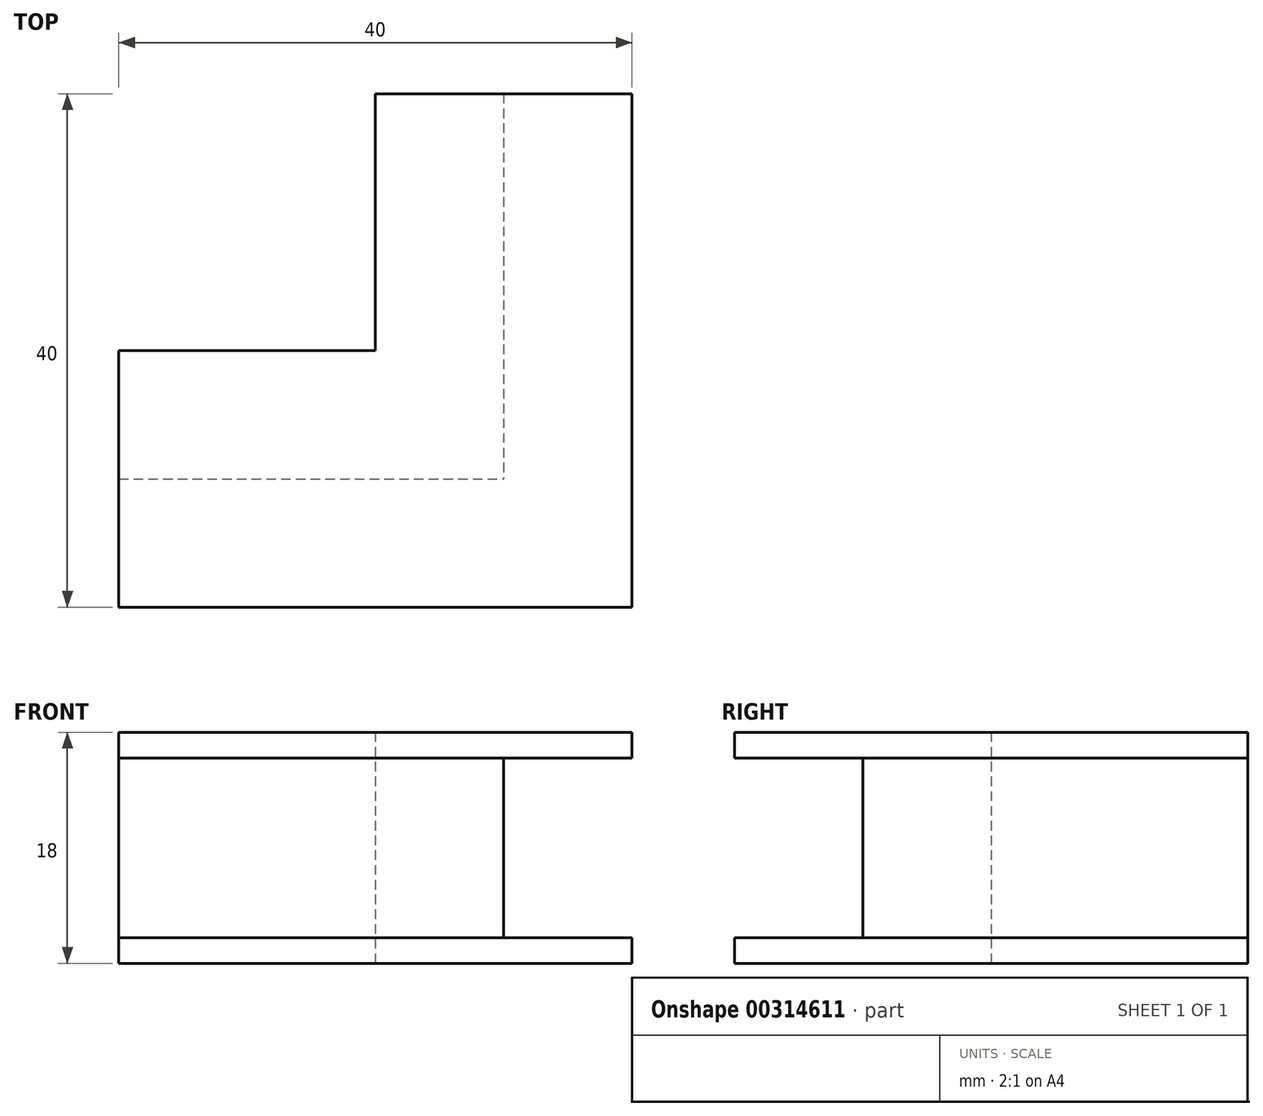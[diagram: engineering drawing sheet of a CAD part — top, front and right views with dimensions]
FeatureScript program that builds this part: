
annotation { "Feature Type Name" : "Feature", "Feature Type Description" : "" }
export const myFeature = defineFeature(function(context is Context, id is Id, definition is map)
    precondition{}
    {
        {
            var Q0;
            Q0=qCreatedBy(makeId("Top.planeOp"),FACE);
            var sketch = newSketch(context, id + "F0", { "sketchPlane" : qUnion([Q0])});
            skLineSegment(sketch, "E0", {"start": v(-10, 30) * mm, "end": v(0, 30) * mm});
            skLineSegment(sketch, "E1", {"start": v(0, 30) * mm, "end": v(0, 0) * mm});
            skLineSegment(sketch, "E2", {"start": v(0, 0) * mm, "end": v(-30, 0) * mm});
            skLineSegment(sketch, "E3", {"start": v(-30, 0) * mm, "end": v(-30, 10) * mm});
            skLineSegment(sketch, "E4", {"start": v(-30, 10) * mm, "end": v(-10, 10) * mm});
            skLineSegment(sketch, "E5", {"start": v(-10, 10) * mm, "end": v(-10, 30) * mm});
            skSolve(sketch);
        }
        {
            var Q0;
            Q0=makeQuery(id+"F0.imprint","IMPRINT",FACE,{"disambiguationData":[TD([[makeQuery(id+"F0.imprint","IMPRINT",EDGE,{"derivedFrom":sQuery(id+"F0.wireOp",EDGE,"E0")}),-1.0]])]});
            extrude(context, id + "F1", {"entities" : qUnion([Q0]), "depth" : 18 * mm});
        }
        {
            var Q0;
            Q0=makeQuery(id+"F1.opExtrude","SWEPT_FACE",FACE,{"disambiguationData":[OSD([sQuery(id+"F0.wireOp",EDGE,"E1")])]});
            var sketch = newSketch(context, id + "F2", { "sketchPlane" : qUnion([Q0])});
            skLineSegment(sketch, "E6.bottom", {"start": v(30, 0) * mm, "end": v(0, 0) * mm});
            skLineSegment(sketch, "E6.top", {"start": v(30, 2) * mm, "end": v(0, 2) * mm});
            skLineSegment(sketch, "E6.left", {"start": v(30, 0) * mm, "end": v(30, 2) * mm});
            skLineSegment(sketch, "E6.right", {"start": v(0, 0) * mm, "end": v(0, 2) * mm});
            skLineSegment(sketch, "E7.bottom", {"start": v(30, 18) * mm, "end": v(0, 18) * mm});
            skLineSegment(sketch, "E7.top", {"start": v(30, 16) * mm, "end": v(0, 16) * mm});
            skLineSegment(sketch, "E7.left", {"start": v(30, 18) * mm, "end": v(30, 16) * mm});
            skLineSegment(sketch, "E7.right", {"start": v(0, 18) * mm, "end": v(0, 16) * mm});
            skSolve(sketch);
        }
        {
            var Q0;
            Q0 = qSketchRegion(id + "F2", true);
            extrude(context, id + "F3", {"entities" : qUnion([Q0]), "operationType" : NewBodyOperationType.ADD, "depth" : 10 * mm});
        }
        {
            var Q0;
            Q0=makeQuery(id+"F3.boolean.opBoolean","MERGE",FACE,{"derivedFrom":[makeQuery(id+"F1.opExtrude","SWEPT_FACE",FACE,{"disambiguationData":[OSD([sQuery(id+"F0.wireOp",EDGE,"E2")])]}),makeQuery(id+"F3.opExtrude","SWEPT_FACE",FACE,{"disambiguationData":[OSD([sQuery(id+"F2.wireOp",EDGE,"E6.right")])]}),makeQuery(id+"F3.opExtrude","SWEPT_FACE",FACE,{"disambiguationData":[OSD([sQuery(id+"F2.wireOp",EDGE,"E7.right")])]})]});
            var sketch = newSketch(context, id + "F4", { "sketchPlane" : qUnion([Q0])});
            skLineSegment(sketch, "E8.bottom", {"start": v(10, 18) * mm, "end": v(-30, 18) * mm});
            skLineSegment(sketch, "E8.top", {"start": v(10, 16) * mm, "end": v(-30, 16) * mm});
            skLineSegment(sketch, "E8.left", {"start": v(10, 18) * mm, "end": v(10, 16) * mm});
            skLineSegment(sketch, "E8.right", {"start": v(-30, 18) * mm, "end": v(-30, 16) * mm});
            skLineSegment(sketch, "E9.bottom", {"start": v(-30, 0) * mm, "end": v(10, 0) * mm});
            skLineSegment(sketch, "E9.top", {"start": v(-30, 2) * mm, "end": v(10, 2) * mm});
            skLineSegment(sketch, "E9.left", {"start": v(-30, 0) * mm, "end": v(-30, 2) * mm});
            skLineSegment(sketch, "E9.right", {"start": v(10, 0) * mm, "end": v(10, 2) * mm});
            skSolve(sketch);
        }
        {
            var Q0;
            Q0 = qSketchRegion(id + "F4", true);
            extrude(context, id + "F5", {"entities" : qUnion([Q0]), "operationType" : NewBodyOperationType.ADD, "depth" : 10 * mm});
        }
    });
